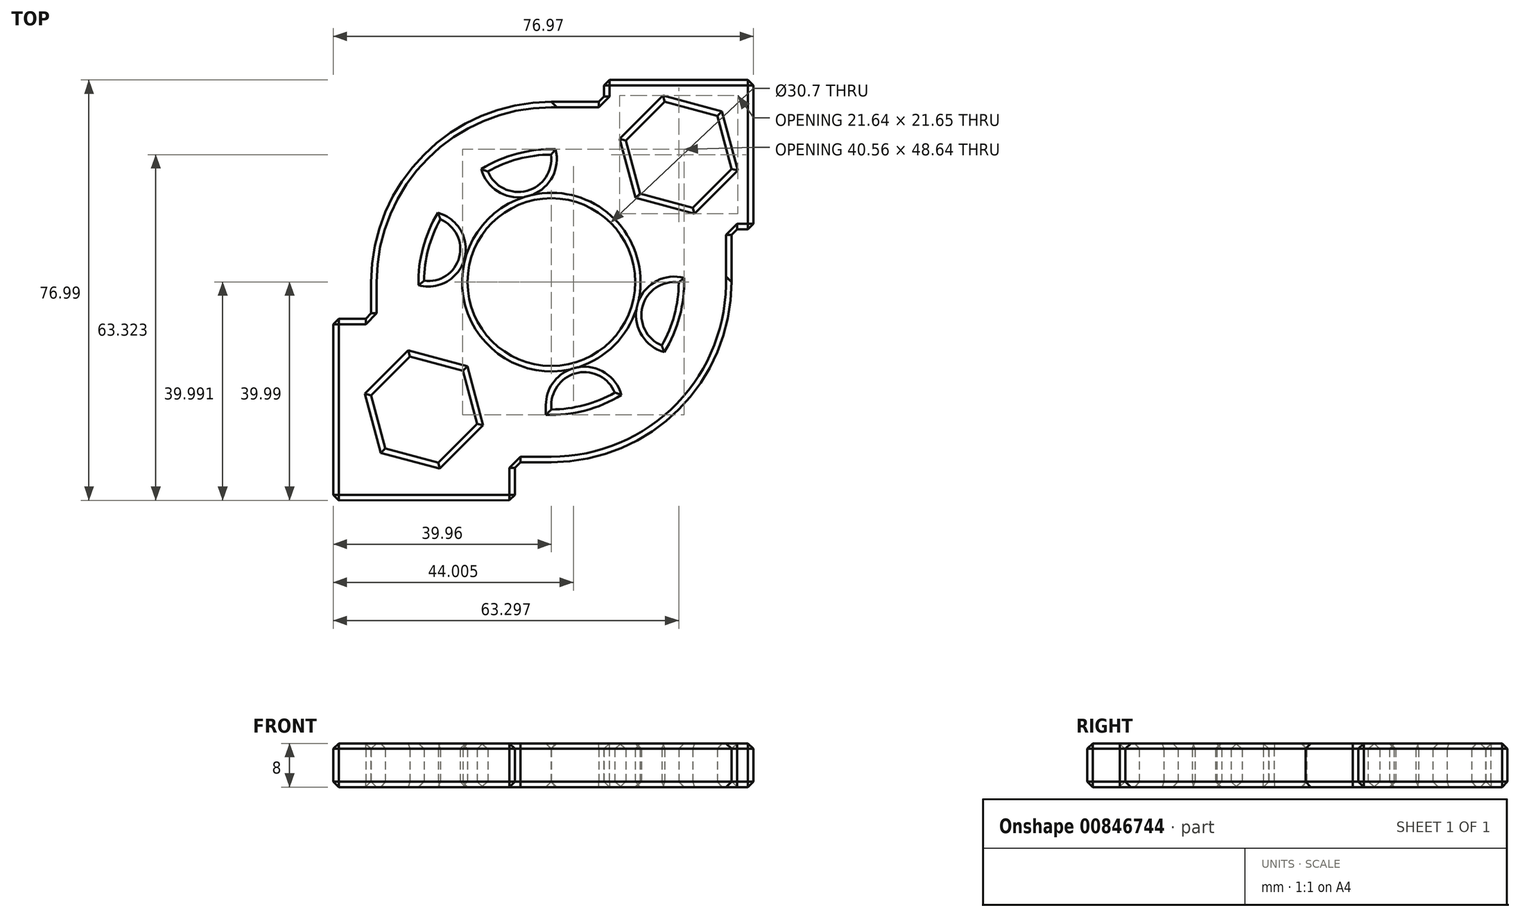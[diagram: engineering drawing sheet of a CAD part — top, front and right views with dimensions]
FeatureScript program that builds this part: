
annotation { "Feature Type Name" : "Feature", "Feature Type Description" : "" }
export const myFeature = defineFeature(function(context is Context, id is Id, definition is map)
    precondition{}
    {
        {
            var Q0;
            Q0=qCreatedBy(makeId("Top.planeOp"),FACE);
            var sketch = newSketch(context, id + "F0", { "sketchPlane" : qUnion([Q0])});
            skCircle(sketch, "E0", {"center": v(0, 0) * mm, "radius": 15.35 * mm});
            skLineSegment(sketch, "E1", {"start": v(0, -33) * mm, "end": v(0, -20.33) * mm});
            skLineSegment(sketch, "E2", {"start": v(0, 16.5) * mm, "end": v(0, 16.5) * mm});
            skCircle(sketch, "E3.cCircle", {"center": v(16.5, 16.5) * mm, "radius": 9.67 * mm, "construction": true});
            skLineSegment(sketch, "E3.0", {"start": v(0, 23.33) * mm, "end": v(0, 33) * mm});
            skLineSegment(sketch, "E3.2", {"start": v(26.17, 16.5) * mm, "end": v(26.17, 16.5) * mm});
            skCircle(sketch, "E4.cCircle", {"center": v(23.34, 23.33) * mm, "radius": 9.67 * mm, "construction": true});
            skLineSegment(sketch, "E4.0", {"start": v(16.5, 26.16) * mm, "end": v(16.5, 26.17) * mm});
            skLineSegment(sketch, "E4.2", {"start": v(30.17, 16.5) * mm, "end": v(30.17, 16.5) * mm});
            skArc(sketch, "E5.cCircle", {"start": v(20.23, -11.62) * mm, "mid": v(-16.5, 16.5) * mm, "end": v(11.62, -20.23) * mm, "construction": true});
            skLineSegment(sketch, "E5.0", {"start": v(16.5, 16.5) * mm, "end": v(16.5, 16.5) * mm});
            skLineSegment(sketch, "E5.1", {"start": v(6.83, -16.5) * mm, "end": v(6.04, -16.5) * mm});
            skCircle(sketch, "E6.cCircle", {"center": v(-16.5, -16.5) * mm, "radius": 23.33 * mm, "construction": true});
            skLineSegment(sketch, "E6.0", {"start": v(0, -20.33) * mm, "end": v(0, -33) * mm});
            skLineSegment(sketch, "E6.1", {"start": v(0, -33) * mm, "end": v(-6.69, -33) * mm});
            skLineSegment(sketch, "E6.3", {"start": v(-33, 0) * mm, "end": v(-23.33, 0) * mm});
            skCircle(sketch, "E7.cCircle", {"center": v(-33.17, -33.43) * mm, "radius": 23.76 * mm, "construction": true});
            skLineSegment(sketch, "E7.0", {"start": v(-16.32, -39.83) * mm, "end": v(-16.32, -39.97) * mm});
            skCircle(sketch, "E8.cCircle", {"center": v(-23.32, -23.35) * mm, "radius": 10.05 * mm, "construction": true});
            skLineSegment(sketch, "E8.0", {"start": v(-16.21, -16.24) * mm, "end": v(-13.61, -25.95) * mm});
            skLineSegment(sketch, "E8.1", {"start": v(-13.61, -25.95) * mm, "end": v(-20.72, -33.06) * mm});
            skLineSegment(sketch, "E8.2", {"start": v(-20.72, -33.06) * mm, "end": v(-30.43, -30.46) * mm});
            skLineSegment(sketch, "E8.3", {"start": v(-30.43, -30.46) * mm, "end": v(-33.03, -20.75) * mm});
            skLineSegment(sketch, "E8.4", {"start": v(-33.03, -20.75) * mm, "end": v(-25.92, -13.64) * mm});
            skLineSegment(sketch, "E8.5", {"start": v(-25.92, -13.64) * mm, "end": v(-16.21, -16.24) * mm});
            skCircle(sketch, "E9.cCircle", {"center": v(23.34, 23.33) * mm, "radius": 10.05 * mm, "construction": true});
            skLineSegment(sketch, "E9.0", {"start": v(16.23, 16.23) * mm, "end": v(13.63, 25.94) * mm});
            skLineSegment(sketch, "E9.1", {"start": v(13.63, 25.94) * mm, "end": v(20.74, 33.04) * mm});
            skLineSegment(sketch, "E9.2", {"start": v(20.74, 33.04) * mm, "end": v(30.44, 30.44) * mm});
            skLineSegment(sketch, "E9.3", {"start": v(30.44, 30.44) * mm, "end": v(33.04, 20.73) * mm});
            skLineSegment(sketch, "E9.4", {"start": v(33.04, 20.73) * mm, "end": v(25.93, 13.62) * mm});
            skLineSegment(sketch, "E9.5", {"start": v(25.93, 13.62) * mm, "end": v(16.23, 16.23) * mm});
            skLineSegment(sketch, "E10.trimOffspring", {"start": v(-33, -6.73) * mm, "end": v(-33, 0) * mm});
            skArc(sketch, "E11.cCircle", {"start": v(-23.33, 0.17) * mm, "mid": v(-27.39, -46.5) * mm, "end": v(-15.3, -1.24) * mm, "construction": true});
            skLineSegment(sketch, "E11.0", {"start": v(-6.69, -33) * mm, "end": v(-6.68, -39.97) * mm});
            skLineSegment(sketch, "E11.1", {"start": v(-6.68, -39.97) * mm, "end": v(-39.94, -39.99) * mm});
            skLineSegment(sketch, "E11.2", {"start": v(-39.94, -39.99) * mm, "end": v(-39.96, -6.73) * mm});
            skLineSegment(sketch, "E11.3", {"start": v(-39.96, -6.73) * mm, "end": v(-33, -6.73) * mm});
            skLineSegment(sketch, "E12.trimOffspring", {"start": v(-39.95, -16.68) * mm, "end": v(-39.83, -16.68) * mm});
            skLineSegment(sketch, "E13.trimOffspring", {"start": v(-16.22, -16.24) * mm, "end": v(-16.22, -16.24) * mm});
            skPoint(sketch, "E14.orphan", {"position": v(-6.7, -6.71) * mm});
            skLineSegment(sketch, "E15.trimOffspring", {"start": v(16.23, 16.23) * mm, "end": v(16.23, 16.23) * mm});
            skPoint(sketch, "E16.orphan", {"position": v(30.17, 30.17) * mm});
            skCircle(sketch, "E17.cCircle", {"center": v(16.5, 16.5) * mm, "radius": 23.34 * mm, "construction": true});
            skLineSegment(sketch, "E17.0", {"start": v(0, 33) * mm, "end": v(0, 33) * mm});
            skLineSegment(sketch, "E17.1", {"start": v(0, 33) * mm, "end": v(9.67, 33) * mm});
            skLineSegment(sketch, "E17.3", {"start": v(33, 0) * mm, "end": v(33, 0) * mm});
            skCircle(sketch, "E18.cCircle", {"center": v(23.34, 23.33) * mm, "radius": 19.33 * mm, "construction": true});
            skLineSegment(sketch, "E18.1", {"start": v(9.67, 37) * mm, "end": v(37, 37) * mm});
            skLineSegment(sketch, "E18.2", {"start": v(37, 37) * mm, "end": v(37, 9.66) * mm});
            skLineSegment(sketch, "E18.3", {"start": v(37, 9.66) * mm, "end": v(33, 9.66) * mm});
            skPoint(sketch, "E19.orphan", {"position": v(9.67, 9.66) * mm});
            skLineSegment(sketch, "E20.trimOffspring", {"start": v(33, 9.66) * mm, "end": v(33, 0) * mm});
            skPoint(sketch, "E21.orphan", {"position": v(33, 16.5) * mm});
            skLineSegment(sketch, "E22.trimOffspring", {"start": v(9.67, 33) * mm, "end": v(9.67, 37) * mm});
            skLineSegment(sketch, "E23.trimOffspring", {"start": v(16.5, 26.17) * mm, "end": v(16.5, 26.16) * mm});
            skPoint(sketch, "E24.orphan", {"position": v(33, 33) * mm});
            skLineSegment(sketch, "E25.trimOffspring", {"start": v(16.5, 0) * mm, "end": v(16.5, 0) * mm});
            skCircle(sketch, "E26", {"center": v(0, 0) * mm, "radius": 23.33 * mm});
            skCircle(sketch, "E27", {"center": v(0, 0) * mm, "radius": 33 * mm});
            skCircle(sketch, "E28", {"center": v(-6.04, 22.54) * mm, "radius": 6.04 * mm});
            skArc(sketch, "E29", {"start": v(-23.33, 0.23) * mm, "mid": v(-16.87, 4.52) * mm, "end": v(-20.32, 11.47) * mm});
            skArc(sketch, "E30", {"start": v(23.33, -0.06) * mm, "mid": v(16.7, -4.48) * mm, "end": v(20.23, -11.62) * mm});
            skArc(sketch, "E31", {"start": v(11.62, -20.23) * mm, "mid": v(1.77, -18.27) * mm, "end": v(3.73, -28.12) * mm});
            skPoint(sketch, "E32.orphan", {"position": v(16.5, -16.5) * mm});
            skPoint(sketch, "E33.orphan", {"position": v(-16.5, 16.5) * mm});
            skLineSegment(sketch, "E34.trimOffspring", {"start": v(0, 22.65) * mm, "end": v(0, 22.43) * mm});
            skPoint(sketch, "E35.start.orphan", {"position": v(0, 33) * mm});
            skSolve(sketch);
        }
        {
            var Q0;
            {var subQ3=sQuery(id+"F0.wireOp",EDGE,"E8.0");var subQ5=sQuery(id+"F0.wireOp",EDGE,"E8.1");var subQ6=makeQuery(id+"F0.imprint","INTERSECT",VERTEX,{"derivedFrom":[subQ3,subQ5]});Q0=makeQuery(id+"F0.imprint","IMPRINT",FACE,{"disambiguationData":[TD([[makeQuery(id+"F0.imprint","IMPRINT",EDGE,{"disambiguationData":[TD([[subQ6,1.0]])],"derivedFrom":subQ3}),1.0]])]});}
            var Q1;
            {var subQ1=sQuery(id+"F0.wireOp",EDGE,"E6.3");var subQ5=sQuery(id+"F0.wireOp",EDGE,"E27");var subQ6=makeQuery(id+"F0.imprint","INTERSECT",VERTEX,{"derivedFrom":[subQ1,subQ5]});Q1=makeQuery(id+"F0.imprint","IMPRINT",FACE,{"disambiguationData":[TD([[makeQuery(id+"F0.imprint","IMPRINT",EDGE,{"disambiguationData":[TD([[subQ6,-1.0]])],"derivedFrom":subQ1}),-1.0]])]});}
            var Q2;
            {var subQ4=sQuery(id+"F0.wireOp",EDGE,"E27");var subQ5=sQuery(id+"F0.wireOp",EDGE,"E3.0");var subQ6=makeQuery(id+"F0.imprint","INTERSECT",VERTEX,{"derivedFrom":[subQ5,subQ4]});Q2=makeQuery(id+"F0.imprint","IMPRINT",FACE,{"disambiguationData":[TD([[makeQuery(id+"F0.imprint","IMPRINT",EDGE,{"disambiguationData":[TD([[subQ6,1.0]])],"derivedFrom":subQ5}),1.0]])]});}
            var Q3;
            {var subQ1=sQuery(id+"F0.wireOp",EDGE,"E9.0");var subQ7=sQuery(id+"F0.wireOp",EDGE,"E9.1");var subQ9=makeQuery(id+"F0.imprint","INTERSECT",VERTEX,{"derivedFrom":[subQ1,subQ7]});Q3=makeQuery(id+"F0.imprint","IMPRINT",FACE,{"disambiguationData":[TD([[makeQuery(id+"F0.imprint","IMPRINT",EDGE,{"disambiguationData":[TD([[subQ9,1.0]])],"derivedFrom":subQ1}),1.0]])]});}
            var Q4;
            {var subQ4=sQuery(id+"F0.wireOp",EDGE,"E6.1");Q4=makeQuery(id+"F0.imprint","IMPRINT",FACE,{"disambiguationData":[TD([[makeQuery(id+"F0.imprint","IMPRINT",EDGE,{"derivedFrom":subQ4}),-1.0]])]});}
            var Q5;
            {var subQ7=sQuery(id+"F0.wireOp",EDGE,"E9.2");Q5=makeQuery(id+"F0.imprint","IMPRINT",FACE,{"disambiguationData":[TD([[makeQuery(id+"F0.imprint","IMPRINT",EDGE,{"derivedFrom":subQ7}),1.0]])]});}
            var Q6;
            {var subQ4=sQuery(id+"F0.wireOp",EDGE,"E17.3");var subQ6=sQuery(id+"F0.wireOp",EDGE,"E27");var subQ8=makeQuery(id+"F0.imprint","INTERSECT",VERTEX,{"derivedFrom":[subQ4,subQ6]});Q6=makeQuery(id+"F0.imprint","IMPRINT",FACE,{"disambiguationData":[TD([[makeQuery(id+"F0.imprint","IMPRINT",EDGE,{"disambiguationData":[TD([[subQ8,-1.0]])],"derivedFrom":subQ4}),1.0]])]});}
            var Q7;
            {var subQ5=sQuery(id+"F0.wireOp",EDGE,"E27");var subQ7=sQuery(id+"F0.wireOp",EDGE,"E3.3");var subQ9=makeQuery(id+"F0.imprint","INTERSECT",VERTEX,{"derivedFrom":[subQ7,subQ5]});Q7=makeQuery(id+"F0.imprint","IMPRINT",FACE,{"disambiguationData":[TD([[makeQuery(id+"F0.imprint","IMPRINT",EDGE,{"disambiguationData":[TD([[subQ9,-1.0]])],"derivedFrom":subQ7}),-1.0]])]});}
            var Q8;
            Q8=makeQuery(id+"F0.imprint","IMPRINT",FACE,{"disambiguationData":[TD([[makeQuery(id+"F0.imprint","IMPRINT",EDGE,{"derivedFrom":sQuery(id+"F0.wireOp",EDGE,"E0")}),-1.0]])]});
            var Q9;
            {var subQ0=sQuery(id+"F0.wireOp",EDGE,"E28");var subQ1=sQuery(id+"F0.wireOp",EDGE,"E26");var subQ2=makeQuery(id+"F0.imprint","INTERSECT",VERTEX,{"disambiguationData":[OD(0.0)],"derivedFrom":[subQ1,subQ0]});Q9=makeQuery(id+"F0.imprint","IMPRINT",FACE,{"disambiguationData":[TD([[makeQuery(id+"F0.imprint","IMPRINT",EDGE,{"disambiguationData":[TD([[subQ2,-1.0]])],"derivedFrom":subQ1}),-1.0]])]});}
            var Q10;
            {var subQ0=sQuery(id+"F0.wireOp",EDGE,"E9.5");var subQ1=sQuery(id+"F0.wireOp",EDGE,"E9.4");var subQ2=makeQuery(id+"F0.imprint","INTERSECT",VERTEX,{"derivedFrom":[subQ1,subQ0]});Q10=makeQuery(id+"F0.imprint","IMPRINT",FACE,{"disambiguationData":[TD([[makeQuery(id+"F0.imprint","IMPRINT",EDGE,{"disambiguationData":[TD([[subQ2,1.0]])],"derivedFrom":subQ1}),1.0]])]});}
            extrude(context, id + "F1", {"entities" : qUnion([Q0, Q1, Q2, Q3, Q4, Q5, Q6, Q7, Q8, Q9, Q10]), "depth" : 8 * mm, "offsetDistance" : 25 * mm});
        }
        {
            var Q0;
            Q0=makeQuery(id+"F1.opExtrude","CAP_EDGE",EDGE,{"disambiguationData":[OSD([sQuery(id+"F0.wireOp",EDGE,"E11.3")])],"isStart":false});
            var Q1;
            Q1=makeQuery(id+"F1.opExtrude","CAP_EDGE",EDGE,{"disambiguationData":[OSD([sQuery(id+"F0.wireOp",EDGE,"E11.2")])],"isStart":false});
            var Q2;
            Q2=makeQuery(id+"F1.opExtrude","CAP_EDGE",EDGE,{"disambiguationData":[OSD([sQuery(id+"F0.wireOp",EDGE,"E11.1")])],"isStart":false});
            var Q3;
            Q3=makeQuery(id+"F1.opExtrude","CAP_EDGE",EDGE,{"disambiguationData":[OSD([sQuery(id+"F0.wireOp",EDGE,"E11.0")])],"isStart":false});
            var Q4;
            {var subQ0=sQuery(id+"F0.wireOp",EDGE,"E27");Q4=makeQuery(id+"F1.opExtrude","CAP_EDGE",EDGE,{"disambiguationData":[OSD([subQ0]),TDD([makeQuery(id+"F0.imprint","IMPRINT",EDGE,{"disambiguationData":[TD([[makeQuery(id+"F0.imprint","INTERSECT",VERTEX,{"derivedFrom":[sQuery(id+"F0.wireOp",EDGE,"E17.3"),subQ0]}),1.0]])],"derivedFrom":subQ0})])],"isStart":false});}
            var Q5;
            Q5=makeQuery(id+"F1.opExtrude","CAP_EDGE",EDGE,{"disambiguationData":[OSD([sQuery(id+"F0.wireOp",EDGE,"E18.2")])],"isStart":false});
            var Q6;
            Q6=makeQuery(id+"F1.opExtrude","CAP_EDGE",EDGE,{"disambiguationData":[OSD([sQuery(id+"F0.wireOp",EDGE,"E18.1")])],"isStart":false});
            var Q7;
            Q7=makeQuery(id+"F1.opExtrude","CAP_EDGE",EDGE,{"disambiguationData":[OSD([sQuery(id+"F0.wireOp",EDGE,"E18.3")])],"isStart":false});
            var Q8;
            Q8=makeQuery(id+"F1.opExtrude","CAP_EDGE",EDGE,{"disambiguationData":[OSD([sQuery(id+"F0.wireOp",EDGE,"E22.trimOffspring")])],"isStart":false});
            var Q9;
            {var subQ0=sQuery(id+"F0.wireOp",EDGE,"E27");var subQ1=makeQuery(id+"F0.imprint","INTERSECT",VERTEX,{"derivedFrom":[sQuery(id+"F0.wireOp",EDGE,"E6.3"),subQ0]});var subQ2=makeQuery(id+"F0.imprint","INTERSECT",VERTEX,{"derivedFrom":[sQuery(id+"F0.wireOp",EDGE,"E3.0"),subQ0]});Q9=makeQuery(id+"F1.opExtrude","CAP_EDGE",EDGE,{"disambiguationData":[OSD([subQ0]),TDD([makeQuery(id+"F0.imprint","IMPRINT",EDGE,{"disambiguationData":[TD([[subQ2,1.0]])],"derivedFrom":subQ0}),makeQuery(id+"F0.imprint","IMPRINT",EDGE,{"disambiguationData":[TD([[subQ2,-1.0]])],"derivedFrom":subQ0}),makeQuery(id+"F0.imprint","IMPRINT",EDGE,{"disambiguationData":[TD([[subQ1,-1.0]])],"derivedFrom":subQ0})])],"isStart":false});}
            var Q10;
            Q10=makeQuery(id+"F1.opExtrude","SWEPT_EDGE",EDGE,{"disambiguationData":[OSD([sQuery(id+"F0.wireOp",EDGE,"E6.1"),sQuery(id+"F0.wireOp",EDGE,"E11.0")])]});
            var Q11;
            Q11=makeQuery(id+"F1.opExtrude","SWEPT_EDGE",EDGE,{"disambiguationData":[OSD([sQuery(id+"F0.wireOp",EDGE,"E6.0"),sQuery(id+"F0.wireOp",EDGE,"E6.1"),sQuery(id+"F0.wireOp",EDGE,"E27")])]});
            var Q12;
            Q12=makeQuery(id+"F1.opExtrude","SWEPT_EDGE",EDGE,{"disambiguationData":[OSD([sQuery(id+"F0.wireOp",EDGE,"E11.0"),sQuery(id+"F0.wireOp",EDGE,"E11.1")])]});
            var Q13;
            Q13=makeQuery(id+"F1.opExtrude","CAP_EDGE",EDGE,{"disambiguationData":[OSD([sQuery(id+"F0.wireOp",EDGE,"E11.0")])],"isStart":true});
            var Q14;
            Q14=makeQuery(id+"F1.opExtrude","CAP_EDGE",EDGE,{"disambiguationData":[OSD([sQuery(id+"F0.wireOp",EDGE,"E11.1")])],"isStart":true});
            var Q15;
            {var subQ0=sQuery(id+"F0.wireOp",EDGE,"E27");var subQ1=makeQuery(id+"F0.imprint","INTERSECT",VERTEX,{"derivedFrom":[sQuery(id+"F0.wireOp",EDGE,"E6.3"),subQ0]});var subQ2=makeQuery(id+"F0.imprint","INTERSECT",VERTEX,{"derivedFrom":[sQuery(id+"F0.wireOp",EDGE,"E3.0"),subQ0]});Q15=makeQuery(id+"F1.opExtrude","CAP_EDGE",EDGE,{"disambiguationData":[OSD([subQ0]),TDD([makeQuery(id+"F0.imprint","IMPRINT",EDGE,{"disambiguationData":[TD([[subQ2,1.0]])],"derivedFrom":subQ0}),makeQuery(id+"F0.imprint","IMPRINT",EDGE,{"disambiguationData":[TD([[subQ2,-1.0]])],"derivedFrom":subQ0}),makeQuery(id+"F0.imprint","IMPRINT",EDGE,{"disambiguationData":[TD([[subQ1,-1.0]])],"derivedFrom":subQ0})])],"isStart":true});}
            var Q16;
            Q16=makeQuery(id+"F1.opExtrude","CAP_FACE",FACE,{"disambiguationData":[OSD([sQuery(id+"F0.wireOp",EDGE,"E0"),sQuery(id+"F0.wireOp",EDGE,"E6.0"),sQuery(id+"F0.wireOp",EDGE,"E6.1"),sQuery(id+"F0.wireOp",EDGE,"E8.0"),sQuery(id+"F0.wireOp",EDGE,"E8.1"),sQuery(id+"F0.wireOp",EDGE,"E8.2"),sQuery(id+"F0.wireOp",EDGE,"E8.3"),sQuery(id+"F0.wireOp",EDGE,"E8.4"),sQuery(id+"F0.wireOp",EDGE,"E8.5"),sQuery(id+"F0.wireOp",EDGE,"E9.0"),sQuery(id+"F0.wireOp",EDGE,"E9.1"),sQuery(id+"F0.wireOp",EDGE,"E9.2"),sQuery(id+"F0.wireOp",EDGE,"E9.3"),sQuery(id+"F0.wireOp",EDGE,"E9.4"),sQuery(id+"F0.wireOp",EDGE,"E9.5"),sQuery(id+"F0.wireOp",EDGE,"E10.trimOffspring"),sQuery(id+"F0.wireOp",EDGE,"E11.0"),sQuery(id+"F0.wireOp",EDGE,"E11.1"),sQuery(id+"F0.wireOp",EDGE,"E11.2"),sQuery(id+"F0.wireOp",EDGE,"E11.3"),sQuery(id+"F0.wireOp",EDGE,"E17.0"),sQuery(id+"F0.wireOp",EDGE,"E17.1"),sQuery(id+"F0.wireOp",EDGE,"E17.3"),sQuery(id+"F0.wireOp",EDGE,"E18.1"),sQuery(id+"F0.wireOp",EDGE,"E18.2"),sQuery(id+"F0.wireOp",EDGE,"E18.3"),sQuery(id+"F0.wireOp",EDGE,"E20.trimOffspring"),sQuery(id+"F0.wireOp",EDGE,"E22.trimOffspring"),sQuery(id+"F0.wireOp",EDGE,"E26"),sQuery(id+"F0.wireOp",EDGE,"E27"),sQuery(id+"F0.wireOp",EDGE,"E28"),sQuery(id+"F0.wireOp",EDGE,"E29"),sQuery(id+"F0.wireOp",EDGE,"E30"),sQuery(id+"F0.wireOp",EDGE,"E31")])],"isStart":true});
            var Q17;
            Q17=makeQuery(id+"F1.opExtrude","SWEPT_EDGE",EDGE,{"disambiguationData":[OSD([sQuery(id+"F0.wireOp",EDGE,"E18.2"),sQuery(id+"F0.wireOp",EDGE,"E18.3")])]});
            var Q18;
            Q18=makeQuery(id+"F1.opExtrude","SWEPT_EDGE",EDGE,{"disambiguationData":[OSD([sQuery(id+"F0.wireOp",EDGE,"E18.1"),sQuery(id+"F0.wireOp",EDGE,"E18.2")])]});
            var Q19;
            Q19=makeQuery(id+"F1.opExtrude","SWEPT_EDGE",EDGE,{"disambiguationData":[OSD([sQuery(id+"F0.wireOp",EDGE,"E18.1"),sQuery(id+"F0.wireOp",EDGE,"E22.trimOffspring")])]});
            var Q20;
            Q20=makeQuery(id+"F1.opExtrude","CAP_FACE",FACE,{"disambiguationData":[OSD([sQuery(id+"F0.wireOp",EDGE,"E0"),sQuery(id+"F0.wireOp",EDGE,"E6.0"),sQuery(id+"F0.wireOp",EDGE,"E6.1"),sQuery(id+"F0.wireOp",EDGE,"E8.0"),sQuery(id+"F0.wireOp",EDGE,"E8.1"),sQuery(id+"F0.wireOp",EDGE,"E8.2"),sQuery(id+"F0.wireOp",EDGE,"E8.3"),sQuery(id+"F0.wireOp",EDGE,"E8.4"),sQuery(id+"F0.wireOp",EDGE,"E8.5"),sQuery(id+"F0.wireOp",EDGE,"E9.0"),sQuery(id+"F0.wireOp",EDGE,"E9.1"),sQuery(id+"F0.wireOp",EDGE,"E9.2"),sQuery(id+"F0.wireOp",EDGE,"E9.3"),sQuery(id+"F0.wireOp",EDGE,"E9.4"),sQuery(id+"F0.wireOp",EDGE,"E9.5"),sQuery(id+"F0.wireOp",EDGE,"E10.trimOffspring"),sQuery(id+"F0.wireOp",EDGE,"E11.0"),sQuery(id+"F0.wireOp",EDGE,"E11.1"),sQuery(id+"F0.wireOp",EDGE,"E11.2"),sQuery(id+"F0.wireOp",EDGE,"E11.3"),sQuery(id+"F0.wireOp",EDGE,"E17.0"),sQuery(id+"F0.wireOp",EDGE,"E17.1"),sQuery(id+"F0.wireOp",EDGE,"E17.3"),sQuery(id+"F0.wireOp",EDGE,"E18.1"),sQuery(id+"F0.wireOp",EDGE,"E18.2"),sQuery(id+"F0.wireOp",EDGE,"E18.3"),sQuery(id+"F0.wireOp",EDGE,"E20.trimOffspring"),sQuery(id+"F0.wireOp",EDGE,"E22.trimOffspring"),sQuery(id+"F0.wireOp",EDGE,"E26"),sQuery(id+"F0.wireOp",EDGE,"E27"),sQuery(id+"F0.wireOp",EDGE,"E28"),sQuery(id+"F0.wireOp",EDGE,"E29"),sQuery(id+"F0.wireOp",EDGE,"E30"),sQuery(id+"F0.wireOp",EDGE,"E31")])],"isStart":false});
            var Q21;
            Q21=makeQuery(id+"F1.opExtrude","SWEPT_EDGE",EDGE,{"disambiguationData":[OSD([sQuery(id+"F0.wireOp",EDGE,"E17.1"),sQuery(id+"F0.wireOp",EDGE,"E22.trimOffspring")])]});
            var Q22;
            Q22=makeQuery(id+"F1.opExtrude","SWEPT_EDGE",EDGE,{"disambiguationData":[OSD([sQuery(id+"F0.wireOp",EDGE,"E10.trimOffspring"),sQuery(id+"F0.wireOp",EDGE,"E11.3")])]});
            var Q23;
            Q23=makeQuery(id+"F1.opExtrude","SWEPT_EDGE",EDGE,{"disambiguationData":[OSD([sQuery(id+"F0.wireOp",EDGE,"E11.2"),sQuery(id+"F0.wireOp",EDGE,"E11.3")])]});
            var Q24;
            Q24=makeQuery(id+"F1.opExtrude","SWEPT_EDGE",EDGE,{"disambiguationData":[OSD([sQuery(id+"F0.wireOp",EDGE,"E11.1"),sQuery(id+"F0.wireOp",EDGE,"E11.2")])]});
            var Q25;
            Q25=makeQuery(id+"F1.opExtrude","SWEPT_EDGE",EDGE,{"disambiguationData":[OSD([sQuery(id+"F0.wireOp",EDGE,"E18.3"),sQuery(id+"F0.wireOp",EDGE,"E20.trimOffspring")])]});
            chamfer(context, id + "F2", {"entities" : qUnion([Q0, Q1, Q2, Q3, Q4, Q5, Q6, Q7, Q8, Q9, Q10, Q11, Q12, Q13, Q14, Q15, Q16, Q17, Q18, Q19, Q20, Q21, Q22, Q23, Q24, Q25]), "width" : 1 * mm, "tangentPropagation" : true});
        }
    });
